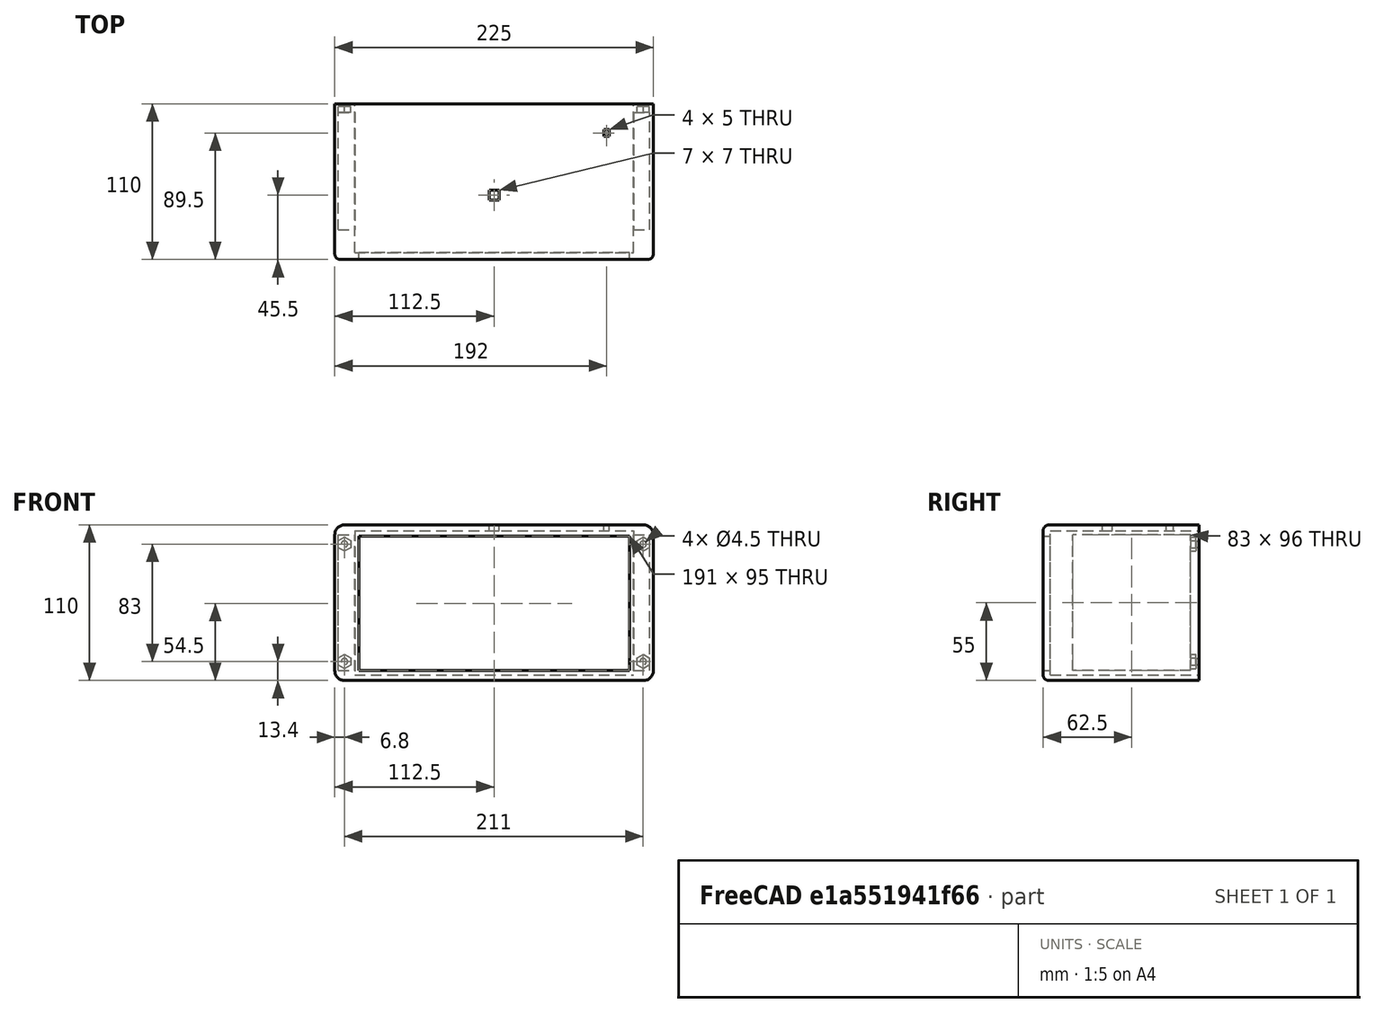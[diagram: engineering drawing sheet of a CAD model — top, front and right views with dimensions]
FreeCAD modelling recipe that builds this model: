
FCSTD DOCUMENT  (FreeCAD 0.18R4 (GitTag))
Label: CADFileProgress4
License: All rights reserved
LicenseURL: http://en.wikipedia.org/wiki/All_rights_reserved
objects: Part::Cut×9, Part::Box×6, Part::Prism×4, Part::Cylinder×4, Part::Fuse×4, Part::Fillet×1
note: 28 computed .brp shape members not serialized (recipe doc carries the construction recipe); baked Part::Feature solids carry a one-line shape summary decoded from their .brp

FEATURE [Part::Box] Box  label="Outer Cube"
  AttacherType = Attacher::AttachEngine3D
  Height = 110
  Length = 225
  Width = 110
FEATURE [Part::Fillet] Fillet
  Base = -> Box
  Edges = 8 edges: [Edge1 r=4,Edge2 r=7,Edge4 r=7,Edge5 r=4,Edge6 r=7,Edge8 r=7,Edge9 r=4,Edge10 r=4]
FEATURE [Part::Box] Box002  label="Inner Cube 1"
  AttacherType = Attacher::AttachEngine3D
  Height = 102
  Length = 197
  Placement = pos=(14,5,4) rot=(0,0,1;0rad)
  Width = 108
FEATURE [Part::Box] Box003  label="Inner Cube 2"
  AttacherType = Attacher::AttachEngine3D
  Height = 95
  Length = 191
  Placement = pos=(17,-3,7) rot=(0,0,1;0rad)
  Width = 50
FEATURE [Part::Cut] Cut
  Base = -> Fillet
  Tool = -> Box003
FEATURE [Part::Cut] Cut001
  Base = -> Cut
  Tool = -> Box002
FEATURE [Part::Prism] Prism
  AttacherType = Attacher::AttachEngine3D
  Circumradius = 5
  Height = 4
  Placement = pos=(6.83013,154,13.4378) rot=(0.935113,-0.250563,-0.250563;4.64535rad)
  Polygon = 6
FEATURE [Part::Box] Box004  label="BoltCuttout"
  AttacherType = Attacher::AttachEngine3D
  Height = 96
  Length = 220
  Placement = pos=(2.5,21,7) rot=(0,0,1;0rad)
  Width = 83
FEATURE [Part::Cut] Cut002
  Base = -> Cut001
  Tool = -> Box004
FEATURE [Part::Cylinder] Cylinder
  Angle = 360
  AttacherType = Attacher::AttachEngine3D
  Height = 2
  Placement = pos=(6.8,158,13.4) rot=(1,0,0;4.71239rad)
  Radius = 2.25
FEATURE [Part::Fuse] Fusion  label="Bottom left Bolt"
  Base = -> Prism
  Placement = pos=(0,-50,0) rot=(0,0,1;0rad)
  Tool = -> Cylinder
FEATURE [Part::Cylinder] Cylinder001
  Angle = 360
  AttacherType = Attacher::AttachEngine3D
  Height = 2
  Placement = pos=(6.8,158,13.4) rot=(-1,0,0;1.5708rad)
  Radius = 2.25
FEATURE [Part::Prism] Prism001
  AttacherType = Attacher::AttachEngine3D
  Circumradius = 5
  Height = 4
  Placement = pos=(6.83013,154,13.4378) rot=(-0.935113,0.250563,0.250563;1.63783rad)
  Polygon = 6
FEATURE [Part::Fuse] Fusion001  label="Top Left Bolt"
  Base = -> Prism001
  Placement = pos=(0,-50,83) rot=(0,0,1;0rad)
  Tool = -> Cylinder001
FEATURE [Part::Cylinder] Cylinder002
  Angle = 360
  AttacherType = Attacher::AttachEngine3D
  Height = 2
  Placement = pos=(6.8,158,13.4) rot=(-1,0,0;1.5708rad)
  Radius = 2.25
FEATURE [Part::Prism] Prism002
  AttacherType = Attacher::AttachEngine3D
  Circumradius = 5
  Height = 4
  Placement = pos=(6.83013,154,13.4378) rot=(-0.935113,0.250563,0.250563;1.63783rad)
  Polygon = 6
FEATURE [Part::Fuse] Fusion002  label="Bottom Right Bolt"
  Base = -> Prism002
  Placement = pos=(211,-50,0) rot=(0,0,1;0rad)
  Tool = -> Cylinder002
FEATURE [Part::Cylinder] Cylinder003
  Angle = 360
  AttacherType = Attacher::AttachEngine3D
  Height = 2
  Placement = pos=(6.8,158,13.4) rot=(-1,0,0;1.5708rad)
  Radius = 2.25
FEATURE [Part::Prism] Prism003
  AttacherType = Attacher::AttachEngine3D
  Circumradius = 5
  Height = 4
  Placement = pos=(6.83013,154,13.4378) rot=(-0.935113,0.250563,0.250563;1.63783rad)
  Polygon = 6
FEATURE [Part::Fuse] Fusion003  label="Top Right Bolt"
  Base = -> Prism003
  Placement = pos=(211,-50,83) rot=(0,0,1;0rad)
  Tool = -> Cylinder003
FEATURE [Part::Cut] Cut003
  Base = -> Cut002
  Tool = -> Fusion
FEATURE [Part::Cut] Cut004
  Base = -> Cut003
  Tool = -> Fusion001
FEATURE [Part::Cut] Cut005
  Base = -> Cut004
  Tool = -> Fusion003
FEATURE [Part::Cut] Cut006
  Base = -> Cut005
  Tool = -> Fusion002
FEATURE [Part::Box] Box005  label="LightSensor"
  AttacherType = Attacher::AttachEngine3D
  Height = 4
  Length = 4
  Placement = pos=(190,87,106) rot=(0,0,1;0rad)
  Width = 5
FEATURE [Part::Box] Box006  label="Button"
  AttacherType = Attacher::AttachEngine3D
  Height = 4
  Length = 7
  Placement = pos=(109,42,106) rot=(0,0,1;0rad)
  Width = 7
FEATURE [Part::Cut] Cut007
  Base = -> Cut006
  Tool = -> Box005
FEATURE [Part::Cut] Cut008
  Base = -> Cut007
  Tool = -> Box006
